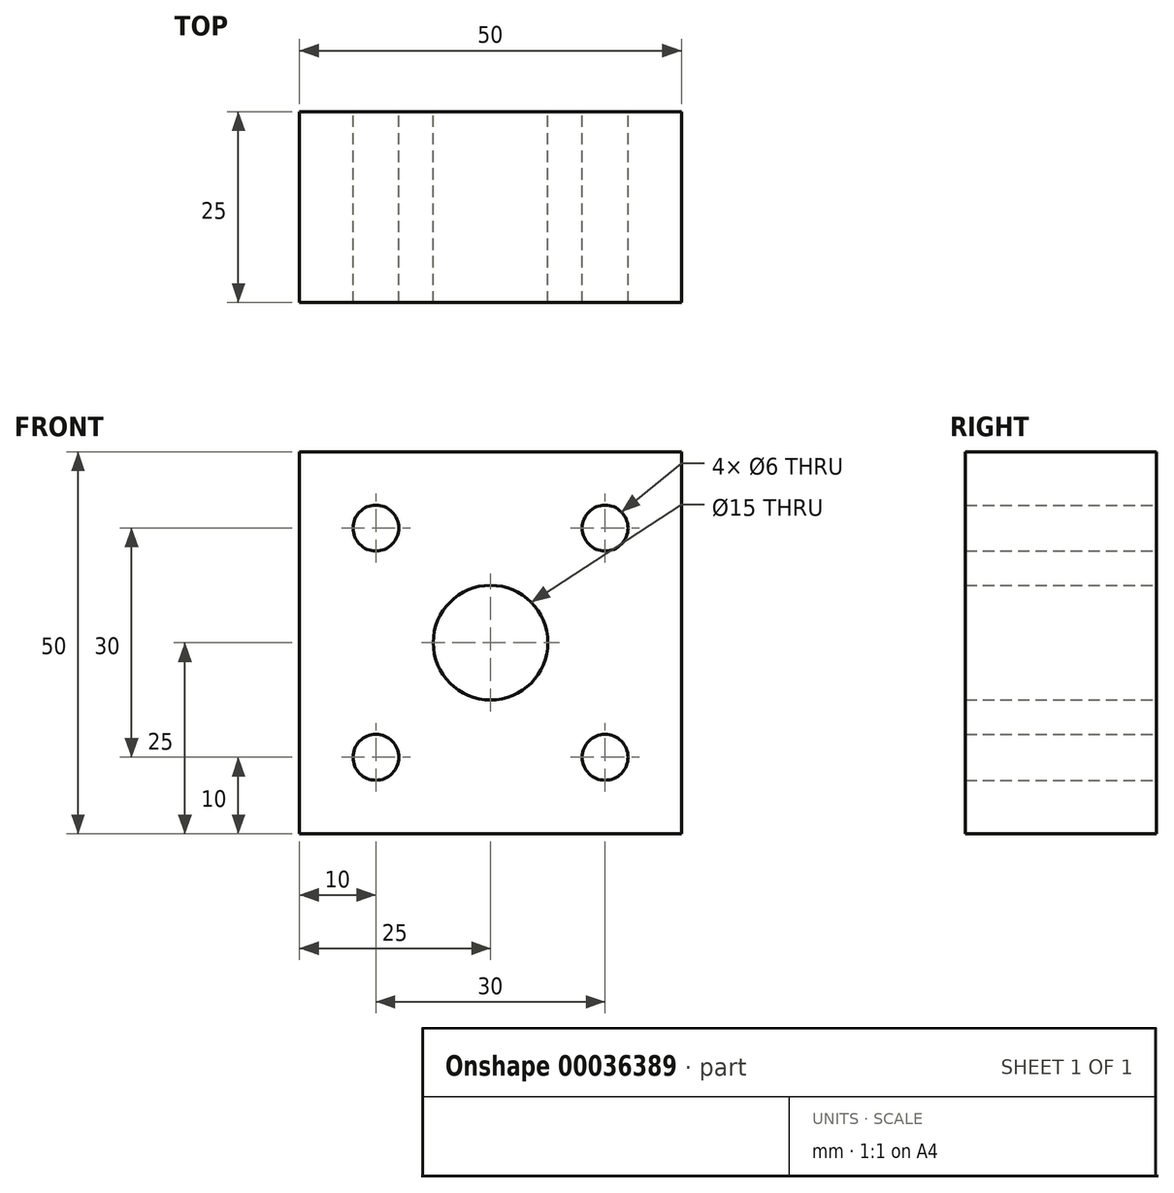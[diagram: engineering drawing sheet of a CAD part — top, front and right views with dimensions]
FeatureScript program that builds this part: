
annotation { "Feature Type Name" : "Feature", "Feature Type Description" : "" }
export const myFeature = defineFeature(function(context is Context, id is Id, definition is map)
    precondition{}
    {
        {
            var Q0;
            Q0=qCreatedBy(makeId("Front.planeOp"),FACE);
            var sketch = newSketch(context, id + "F0", { "sketchPlane" : qUnion([Q0])});
            skLineSegment(sketch, "E0.rect.bottom", {"start": v(-25, 25) * mm, "end": v(25, 25) * mm});
            skLineSegment(sketch, "E0.rect.top", {"start": v(-25, -25) * mm, "end": v(25, -25) * mm});
            skLineSegment(sketch, "E0.rect.left", {"start": v(-25, 25) * mm, "end": v(-25, -25) * mm});
            skLineSegment(sketch, "E0.rect.right", {"start": v(25, 25) * mm, "end": v(25, -25) * mm});
            skPoint(sketch, "E0.rect.middle", {"position": v(0, 0) * mm});
            skCircle(sketch, "E1", {"center": v(0, 0) * mm, "radius": 7.5 * mm});
            skCircle(sketch, "E2", {"center": v(-15, 15) * mm, "radius": 3 * mm});
            skCircle(sketch, "E3", {"center": v(15, 15) * mm, "radius": 3 * mm});
            skCircle(sketch, "E4", {"center": v(-15, -15) * mm, "radius": 3 * mm});
            skCircle(sketch, "E5", {"center": v(15, -15) * mm, "radius": 3 * mm});
            skLineSegment(sketch, "E6.rect.bottom", {"start": v(-15, 15) * mm, "end": v(15, 15) * mm, "construction": true});
            skLineSegment(sketch, "E6.rect.top", {"start": v(-15, -15) * mm, "end": v(15, -15) * mm, "construction": true});
            skLineSegment(sketch, "E6.rect.left", {"start": v(-15, 15) * mm, "end": v(-15, -15) * mm, "construction": true});
            skLineSegment(sketch, "E6.rect.right", {"start": v(15, 15) * mm, "end": v(15, -15) * mm, "construction": true});
            skSolve(sketch);
        }
        {
            var Q0;
            Q0=makeQuery(id+"F0.imprint","IMPRINT",FACE,{"disambiguationData":[TD([[makeQuery(id+"F0.imprint","IMPRINT",EDGE,{"derivedFrom":sQuery(id+"F0.wireOp",EDGE,"E0.rect.bottom")}),-1.0]])]});
            extrude(context, id + "F1", {"entities" : qUnion([Q0]), "depth" : 25 * mm});
        }
    });
